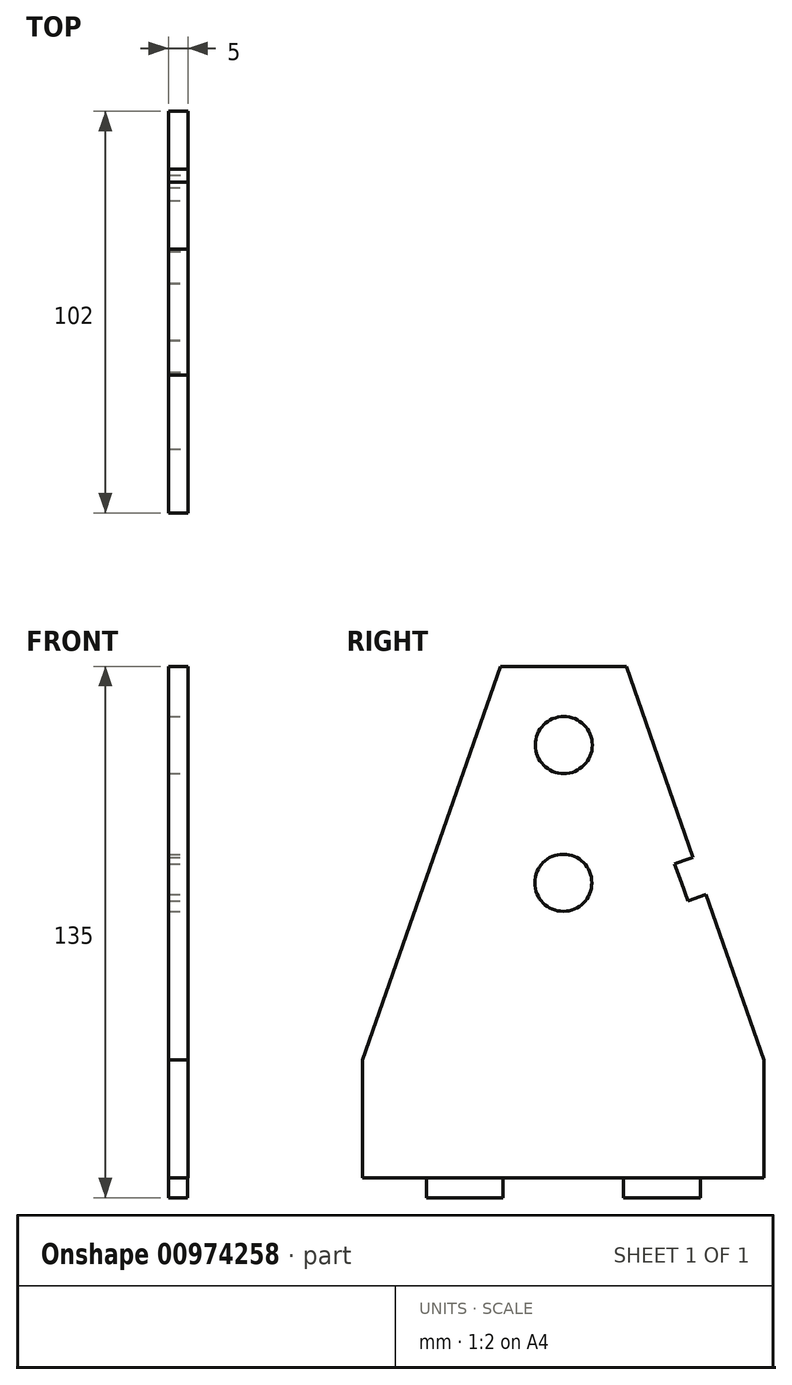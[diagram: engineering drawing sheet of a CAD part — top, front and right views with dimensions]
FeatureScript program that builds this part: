
annotation { "Feature Type Name" : "Feature", "Feature Type Description" : "" }
export const myFeature = defineFeature(function(context is Context, id is Id, definition is map)
    precondition{}
    {
        {
            var Q0;
            Q0=qCreatedBy(makeId("Top.planeOp"),FACE);
            var sketch = newSketch(context, id + "F0", { "sketchPlane" : qUnion([Q0])});
            skLineSegment(sketch, "E0", {"start": v(0, 39.57) * mm, "end": v(0, -62.43) * mm});
            skLineSegment(sketch, "E1", {"start": v(5, 39.57) * mm, "end": v(5, -62.43) * mm});
            skLineSegment(sketch, "E2", {"start": v(0, 39.57) * mm, "end": v(5, 39.57) * mm});
            skLineSegment(sketch, "E3", {"start": v(0, -62.43) * mm, "end": v(5, -62.43) * mm});
            skLineSegment(sketch, "E4", {"start": v(-6.9, 23.37) * mm, "end": v(13.87, 23.37) * mm});
            skLineSegment(sketch, "E5", {"start": v(-6.9, 3.87) * mm, "end": v(13.87, 3.87) * mm});
            skLineSegment(sketch, "E6.MirrorCS", {"start": v(-6.9, -26.73) * mm, "end": v(13.87, -26.73) * mm});
            skLineSegment(sketch, "E7.MirrorCS", {"start": v(-6.9, -46.23) * mm, "end": v(13.87, -46.23) * mm});
            skLineSegment(sketch, "E8", {"start": v(0.1, 39.57) * mm, "end": v(0.1, -62.43) * mm});
            skLineSegment(sketch, "E9", {"start": v(4.9, -62.43) * mm, "end": v(4.9, 39.57) * mm});
            skSolve(sketch);
        }
        {
            var Q0;
            {var subQ0=sQuery(id+"F0.wireOp",EDGE,"E8");var subQ1=sQuery(id+"F0.wireOp",EDGE,"E3");var subQ2=makeQuery(id+"F0.imprint","INTERSECT",VERTEX,{"derivedFrom":[subQ1,subQ0]});Q0=makeQuery(id+"F0.imprint","IMPRINT",FACE,{"disambiguationData":[TD([[makeQuery(id+"F0.imprint","IMPRINT",EDGE,{"disambiguationData":[TD([[subQ2,-1.0]])],"derivedFrom":subQ1}),1.0]])]});}
            var Q1;
            {var subQ0=sQuery(id+"F0.wireOp",EDGE,"E8");var subQ1=sQuery(id+"F0.wireOp",EDGE,"E6.MirrorCS");var subQ2=makeQuery(id+"F0.imprint","INTERSECT",VERTEX,{"derivedFrom":[subQ1,subQ0]});Q1=makeQuery(id+"F0.imprint","IMPRINT",FACE,{"disambiguationData":[TD([[makeQuery(id+"F0.imprint","IMPRINT",EDGE,{"disambiguationData":[TD([[subQ2,-1.0]])],"derivedFrom":subQ1}),-1.0]])]});}
            var Q2;
            {var subQ0=sQuery(id+"F0.wireOp",EDGE,"E8");var subQ1=sQuery(id+"F0.wireOp",EDGE,"E5");var subQ2=makeQuery(id+"F0.imprint","INTERSECT",VERTEX,{"derivedFrom":[subQ1,subQ0]});Q2=makeQuery(id+"F0.imprint","IMPRINT",FACE,{"disambiguationData":[TD([[makeQuery(id+"F0.imprint","IMPRINT",EDGE,{"disambiguationData":[TD([[subQ2,-1.0]])],"derivedFrom":subQ1}),-1.0]])]});}
            var Q3;
            {var subQ0=sQuery(id+"F0.wireOp",EDGE,"E8");var subQ1=sQuery(id+"F0.wireOp",EDGE,"E4");var subQ2=makeQuery(id+"F0.imprint","INTERSECT",VERTEX,{"derivedFrom":[subQ1,subQ0]});Q3=makeQuery(id+"F0.imprint","IMPRINT",FACE,{"disambiguationData":[TD([[makeQuery(id+"F0.imprint","IMPRINT",EDGE,{"disambiguationData":[TD([[subQ2,-1.0]])],"derivedFrom":subQ1}),-1.0]])]});}
            var Q4;
            {var subQ0=sQuery(id+"F0.wireOp",EDGE,"E8");var subQ1=sQuery(id+"F0.wireOp",EDGE,"E2");var subQ2=makeQuery(id+"F0.imprint","INTERSECT",VERTEX,{"derivedFrom":[subQ1,subQ0]});Q4=makeQuery(id+"F0.imprint","IMPRINT",FACE,{"disambiguationData":[TD([[makeQuery(id+"F0.imprint","IMPRINT",EDGE,{"disambiguationData":[TD([[subQ2,-1.0]])],"derivedFrom":subQ1}),-1.0]])]});}
            var Q5;
            {var subQ0=sQuery(id+"F0.wireOp",EDGE,"E1");var subQ1=sQuery(id+"F0.wireOp",EDGE,"E6.MirrorCS");var subQ2=makeQuery(id+"F0.imprint","INTERSECT",VERTEX,{"derivedFrom":[subQ1,subQ0]});Q5=makeQuery(id+"F0.imprint","IMPRINT",FACE,{"disambiguationData":[TD([[makeQuery(id+"F0.imprint","IMPRINT",EDGE,{"disambiguationData":[TD([[subQ2,1.0]])],"derivedFrom":subQ1}),-1.0]])]});}
            var Q6;
            {var subQ0=sQuery(id+"F0.wireOp",EDGE,"E1");var subQ1=sQuery(id+"F0.wireOp",EDGE,"E3");var subQ2=makeQuery(id+"F0.imprint","INTERSECT",VERTEX,{"derivedFrom":[subQ1,subQ0]});Q6=makeQuery(id+"F0.imprint","IMPRINT",FACE,{"disambiguationData":[TD([[makeQuery(id+"F0.imprint","IMPRINT",EDGE,{"disambiguationData":[TD([[subQ2,1.0]])],"derivedFrom":subQ1}),1.0]])]});}
            var Q7;
            {var subQ0=sQuery(id+"F0.wireOp",EDGE,"E0");var subQ1=sQuery(id+"F0.wireOp",EDGE,"E3");var subQ2=makeQuery(id+"F0.imprint","INTERSECT",VERTEX,{"derivedFrom":[subQ1,subQ0]});Q7=makeQuery(id+"F0.imprint","IMPRINT",FACE,{"disambiguationData":[TD([[makeQuery(id+"F0.imprint","IMPRINT",EDGE,{"disambiguationData":[TD([[subQ2,-1.0]])],"derivedFrom":subQ1}),1.0]])]});}
            var Q8;
            {var subQ0=sQuery(id+"F0.wireOp",EDGE,"E0");var subQ1=sQuery(id+"F0.wireOp",EDGE,"E6.MirrorCS");var subQ2=makeQuery(id+"F0.imprint","INTERSECT",VERTEX,{"derivedFrom":[subQ1,subQ0]});Q8=makeQuery(id+"F0.imprint","IMPRINT",FACE,{"disambiguationData":[TD([[makeQuery(id+"F0.imprint","IMPRINT",EDGE,{"disambiguationData":[TD([[subQ2,-1.0]])],"derivedFrom":subQ1}),-1.0]])]});}
            var Q9;
            {var subQ0=sQuery(id+"F0.wireOp",EDGE,"E0");var subQ1=sQuery(id+"F0.wireOp",EDGE,"E5");var subQ2=makeQuery(id+"F0.imprint","INTERSECT",VERTEX,{"derivedFrom":[subQ1,subQ0]});Q9=makeQuery(id+"F0.imprint","IMPRINT",FACE,{"disambiguationData":[TD([[makeQuery(id+"F0.imprint","IMPRINT",EDGE,{"disambiguationData":[TD([[subQ2,-1.0]])],"derivedFrom":subQ1}),-1.0]])]});}
            var Q10;
            {var subQ0=sQuery(id+"F0.wireOp",EDGE,"E1");var subQ1=sQuery(id+"F0.wireOp",EDGE,"E5");var subQ2=makeQuery(id+"F0.imprint","INTERSECT",VERTEX,{"derivedFrom":[subQ1,subQ0]});Q10=makeQuery(id+"F0.imprint","IMPRINT",FACE,{"disambiguationData":[TD([[makeQuery(id+"F0.imprint","IMPRINT",EDGE,{"disambiguationData":[TD([[subQ2,1.0]])],"derivedFrom":subQ1}),-1.0]])]});}
            var Q11;
            {var subQ0=sQuery(id+"F0.wireOp",EDGE,"E1");var subQ1=sQuery(id+"F0.wireOp",EDGE,"E4");var subQ2=makeQuery(id+"F0.imprint","INTERSECT",VERTEX,{"derivedFrom":[subQ1,subQ0]});Q11=makeQuery(id+"F0.imprint","IMPRINT",FACE,{"disambiguationData":[TD([[makeQuery(id+"F0.imprint","IMPRINT",EDGE,{"disambiguationData":[TD([[subQ2,1.0]])],"derivedFrom":subQ1}),-1.0]])]});}
            var Q12;
            {var subQ0=sQuery(id+"F0.wireOp",EDGE,"E0");var subQ1=sQuery(id+"F0.wireOp",EDGE,"E4");var subQ2=makeQuery(id+"F0.imprint","INTERSECT",VERTEX,{"derivedFrom":[subQ1,subQ0]});Q12=makeQuery(id+"F0.imprint","IMPRINT",FACE,{"disambiguationData":[TD([[makeQuery(id+"F0.imprint","IMPRINT",EDGE,{"disambiguationData":[TD([[subQ2,-1.0]])],"derivedFrom":subQ1}),-1.0]])]});}
            var Q13;
            {var subQ0=sQuery(id+"F0.wireOp",EDGE,"E0");var subQ1=sQuery(id+"F0.wireOp",EDGE,"E2");var subQ2=makeQuery(id+"F0.imprint","INTERSECT",VERTEX,{"derivedFrom":[subQ1,subQ0]});Q13=makeQuery(id+"F0.imprint","IMPRINT",FACE,{"disambiguationData":[TD([[makeQuery(id+"F0.imprint","IMPRINT",EDGE,{"disambiguationData":[TD([[subQ2,-1.0]])],"derivedFrom":subQ1}),-1.0]])]});}
            var Q14;
            {var subQ0=sQuery(id+"F0.wireOp",EDGE,"E1");var subQ1=sQuery(id+"F0.wireOp",EDGE,"E2");var subQ2=makeQuery(id+"F0.imprint","INTERSECT",VERTEX,{"derivedFrom":[subQ1,subQ0]});Q14=makeQuery(id+"F0.imprint","IMPRINT",FACE,{"disambiguationData":[TD([[makeQuery(id+"F0.imprint","IMPRINT",EDGE,{"disambiguationData":[TD([[subQ2,1.0]])],"derivedFrom":subQ1}),-1.0]])]});}
            extrude(context, id + "F1", {"entities" : qUnion([Q0, Q1, Q2, Q3, Q4, Q5, Q6, Q7, Q8, Q9, Q10, Q11, Q12, Q13, Q14]), "depth" : 130 * mm, "offsetDistance" : 25 * mm});
        }
        {
            var Q0;
            {var subQ0=sQuery(id+"F0.wireOp",EDGE,"E8");var subQ1=sQuery(id+"F0.wireOp",EDGE,"E6.MirrorCS");var subQ2=makeQuery(id+"F0.imprint","INTERSECT",VERTEX,{"derivedFrom":[subQ1,subQ0]});Q0=makeQuery(id+"F0.imprint","IMPRINT",FACE,{"disambiguationData":[TD([[makeQuery(id+"F0.imprint","IMPRINT",EDGE,{"disambiguationData":[TD([[subQ2,-1.0]])],"derivedFrom":subQ1}),-1.0]])]});}
            var Q1;
            {var subQ0=sQuery(id+"F0.wireOp",EDGE,"E8");var subQ1=sQuery(id+"F0.wireOp",EDGE,"E4");var subQ2=makeQuery(id+"F0.imprint","INTERSECT",VERTEX,{"derivedFrom":[subQ1,subQ0]});Q1=makeQuery(id+"F0.imprint","IMPRINT",FACE,{"disambiguationData":[TD([[makeQuery(id+"F0.imprint","IMPRINT",EDGE,{"disambiguationData":[TD([[subQ2,-1.0]])],"derivedFrom":subQ1}),-1.0]])]});}
            extrude(context, id + "F2", {"entities" : qUnion([Q0, Q1]), "operationType" : NewBodyOperationType.ADD, "depth" : -5 * mm, "offsetDistance" : 25 * mm});
        }
        {
            var Q0;
            Q0=makeQuery(id+"F1.opExtrude","CAP_EDGE",EDGE,{"disambiguationData":[OSD([sQuery(id+"F0.wireOp",EDGE,"E3")])],"isStart":false});
            var Q1;
            Q1=makeQuery(id+"F1.opExtrude","CAP_EDGE",EDGE,{"disambiguationData":[OSD([sQuery(id+"F0.wireOp",EDGE,"E2")])],"isStart":false});
            chamfer(context, id + "F3", {"entities" : qUnion([Q0, Q1]), "chamferType" : ChamferType.TWO_OFFSETS, "width1" : 35 * mm, "oppositeDirection" : false, "width2" : 100 * mm, "tangentPropagation" : true});
        }
        {
            var Q0;
            Q0=makeQuery(id+"F1.opExtrude","SWEPT_FACE",FACE,{"disambiguationData":[OSD([sQuery(id+"F0.wireOp",EDGE,"E1")])]});
            var sketch = newSketch(context, id + "F4", { "sketchPlane" : qUnion([Q0])});
            skLineSegment(sketch, "E10", {"start": v(-62.43, 0) * mm, "end": v(39.57, 0) * mm, "construction": true});
            skLineSegment(sketch, "E11", {"start": v(-62.43, 75) * mm, "end": v(39.57, 75) * mm, "construction": true});
            skLineSegment(sketch, "E12", {"start": v(-11.32, 0) * mm, "end": v(-11.43, 75) * mm, "construction": true});
            skPoint(sketch, "E12.endSnap0", {"position": v(-11.43, 75) * mm});
            skLineSegment(sketch, "E13", {"start": v(39.57, 110) * mm, "end": v(-62.43, 110) * mm, "construction": true});
            skLineSegment(sketch, "E14", {"start": v(-11.43, 75) * mm, "end": v(-11.32, 110) * mm, "construction": true});
            skPoint(sketch, "E15", {"position": v(-11.32, 110) * mm});
            skLineSegment(sketch, "E16", {"start": v(-22.13, 130) * mm, "end": v(-62.43, 14.86) * mm, "construction": true});
            skLineSegment(sketch, "E17", {"start": v(-41.38, 75) * mm, "end": v(-43.74, 75.83) * mm, "construction": true});
            skLineSegment(sketch, "E18", {"start": v(-39.73, 79.72) * mm, "end": v(-44.45, 81.37) * mm});
            skLineSegment(sketch, "E19.MirrorCS", {"start": v(-39.73, 79.72) * mm, "end": v(-42.1, 80.55) * mm});
            skLineSegment(sketch, "E20", {"start": v(-43.03, 70.28) * mm, "end": v(-47.75, 71.93) * mm});
            skLineSegment(sketch, "E21.MirrorCS", {"start": v(-0.9, 130.03) * mm, "end": v(39.75, 15.02) * mm, "construction": true});
            skLineSegment(sketch, "E22.MirrorCS", {"start": v(16.86, 79.8) * mm, "end": v(19.21, 80.64) * mm});
            skLineSegment(sketch, "E23.MirrorCS", {"start": v(18.52, 75.09) * mm, "end": v(20.88, 75.92) * mm, "construction": true});
            skLineSegment(sketch, "E24.MirrorCS", {"start": v(20.19, 70.37) * mm, "end": v(24.9, 72.04) * mm});
            skLineSegment(sketch, "E25", {"start": v(-39.73, 79.72) * mm, "end": v(-43.03, 70.28) * mm});
            skLineSegment(sketch, "E26", {"start": v(18.52, 75.09) * mm, "end": v(20.19, 70.37) * mm});
            skLineSegment(sketch, "E27", {"start": v(18.52, 75.09) * mm, "end": v(16.86, 79.8) * mm});
            skLineSegment(sketch, "E28", {"start": v(19.21, 80.64) * mm, "end": v(21.56, 81.46) * mm});
            skSolve(sketch);
        }
        {
            var Q0;
            Q0=sQuery(id+"F4.wireOp",VERTEX,"E12.endSnap0");
            var Q1;
            Q1=sQuery(id+"F4.wireOp",VERTEX,"E15");
            var Q2;
            Q2=makeQuery(id+"F1.opExtrude","SWEPT_BODY",BODY,{"disambiguationData":[OSD([sQuery(id+"F0.wireOp",EDGE,"E2"),sQuery(id+"F0.wireOp",EDGE,"E3"),sQuery(id+"F0.wireOp",EDGE,"E0"),sQuery(id+"F0.wireOp",EDGE,"E1")])]});
            hole(context, id + "F5", {"style" : HoleStyle.SIMPLE, "endStyle" : HoleEndStyle.THROUGH, "holeDiameter" : 14.5 * mm, "majorDiameter" : 5 * mm, "isTappedThrough" : true, "tappedDepth" : 12 * mm, "tapClearance" : 3, "locations" : qUnion([Q0, Q1]), "scope" : qUnion([Q2])});
        }
        {
            var Q0;
            {var subQ0=sQuery(id+"F4.wireOp",EDGE,"E20");Q0=makeQuery(id+"F4.imprint","IMPRINT",FACE,{"disambiguationData":[TD([[makeQuery(id+"F4.imprint","IMPRINT",EDGE,{"derivedFrom":subQ0}),-1.0]])]});}
            var Q1;
            Q1=makeQuery(id+"F4.imprint","IMPRINT",FACE,{"disambiguationData":[TD([[makeQuery(id+"F4.imprint","IMPRINT",EDGE,{"derivedFrom":sQuery(id+"F4.wireOp",EDGE,"E22.MirrorCS")}),-1.0]])]});
            extrude(context, id + "F6", {"entities" : qUnion([Q0, Q1]), "operationType" : NewBodyOperationType.REMOVE, "oppositeDirection" : true, "depth" : 25 * mm, "offsetDistance" : 25 * mm});
        }
    });
